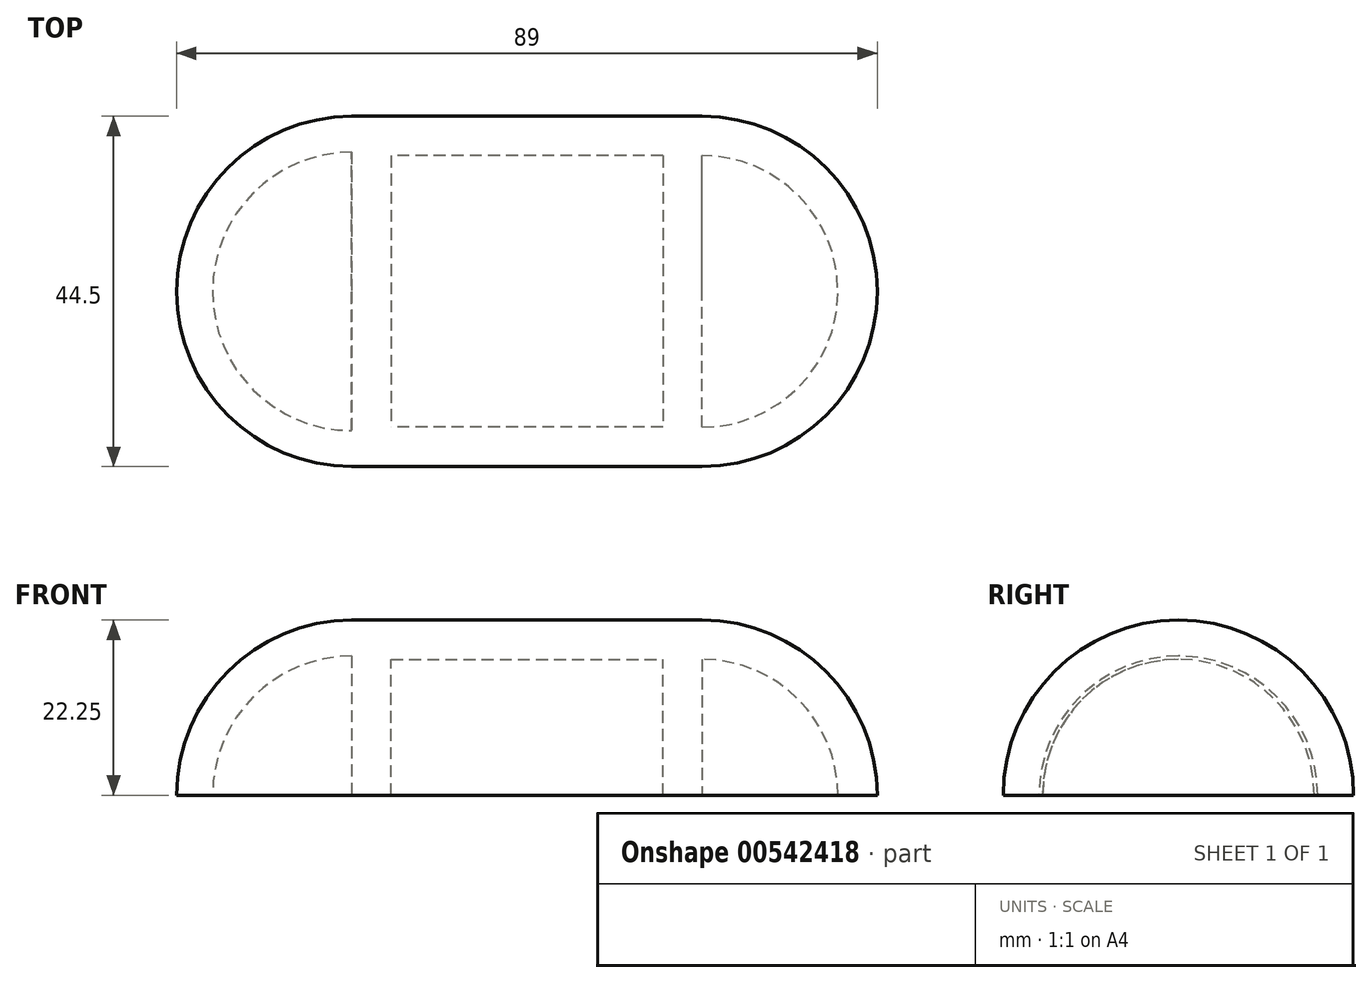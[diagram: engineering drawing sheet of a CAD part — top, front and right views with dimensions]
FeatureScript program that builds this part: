
annotation { "Feature Type Name" : "Feature", "Feature Type Description" : "" }
export const myFeature = defineFeature(function(context is Context, id is Id, definition is map)
    precondition{}
    {
        {
            var Q0;
            Q0=qCreatedBy(makeId("Top.planeOp"),FACE);
            var sketch = newSketch(context, id + "F0", { "sketchPlane" : qUnion([Q0])});
            skLineSegment(sketch, "E0.bottom", {"start": v(22.25, 22.25) * mm, "end": v(-22.25, 22.25) * mm});
            skLineSegment(sketch, "E0.top", {"start": v(22.25, -22.25) * mm, "end": v(-22.25, -22.25) * mm});
            skLineSegment(sketch, "E0.left", {"start": v(22.25, 22.25) * mm, "end": v(22.25, -22.25) * mm});
            skLineSegment(sketch, "E0.right", {"start": v(-22.25, 22.25) * mm, "end": v(-22.25, -22.25) * mm});
            skPoint(sketch, "E0.middle", {"position": v(0, 0) * mm});
            skLineSegment(sketch, "E1.bottom", {"start": v(17.25, -17.25) * mm, "end": v(-17.25, -17.25) * mm});
            skLineSegment(sketch, "E1.top", {"start": v(17.25, 17.25) * mm, "end": v(-17.25, 17.25) * mm});
            skLineSegment(sketch, "E1.left", {"start": v(17.25, -17.25) * mm, "end": v(17.25, 17.25) * mm});
            skLineSegment(sketch, "E1.right", {"start": v(-17.25, -17.25) * mm, "end": v(-17.25, 17.25) * mm});
            skLineSegment(sketch, "E2", {"start": v(-45.54, 0) * mm, "end": v(54.8, 0) * mm});
            skPoint(sketch, "E2.endSnap0", {"position": v(-22.25, 0) * mm});
            skSolve(sketch);
        }
        {
            var Q0;
            {var subQ1=sQuery(id+"F0.wireOp",EDGE,"E0.top");Q0=makeQuery(id+"F0.imprint","IMPRINT",FACE,{"disambiguationData":[TD([[makeQuery(id+"F0.imprint","IMPRINT",EDGE,{"derivedFrom":subQ1}),-1.0]])]});}
            var Q1;
            Q1=sQuery(id+"F0.wireOp",EDGE,"E2");
            revolve(context, id + "F1", {"entities" : qUnion([Q0]), "axis" : qUnion([Q1]), "revolveType" : RevolveType.ONE_DIRECTION, "oppositeDirection" : true, "angle" : 180 * degree});
        }
        {
            var Q0;
            Q0=makeQuery(id+"F1.opRevolve","SWEPT_FACE",FACE,{"disambiguationData":[OSD([sQuery(id+"F0.wireOp",EDGE,"E0.left")])]});
            var sketch = newSketch(context, id + "F2", { "sketchPlane" : qUnion([Q0])});
            skArc(sketch, "E3", {"start": v(-22.25, 0) * mm, "mid": v(-15.73, 15.73) * mm, "end": v(0, 22.25) * mm});
            skArc(sketch, "E4", {"start": v(-17.25, 0) * mm, "mid": v(-12.2, 12.2) * mm, "end": v(0, 17.25) * mm});
            skLineSegment(sketch, "E5", {"start": v(-32.26, 0) * mm, "end": v(44.71, 0) * mm});
            skLineSegment(sketch, "E6", {"start": v(0, 30.6) * mm, "end": v(0, -10.44) * mm});
            skSolve(sketch);
        }
        {
            var Q0;
            {var subQ0=sQuery(id+"F2.wireOp",EDGE,"E3");Q0=makeQuery(id+"F2.imprint","IMPRINT",FACE,{"disambiguationData":[TD([[makeQuery(id+"F2.imprint","IMPRINT",EDGE,{"derivedFrom":subQ0}),1.0]])]});}
            var Q1;
            Q1=sQuery(id+"F2.wireOp",EDGE,"E6");
            revolve(context, id + "F3", {"operationType" : NewBodyOperationType.ADD, "entities" : qUnion([Q0]), "axis" : qUnion([Q1]), "revolveType" : RevolveType.ONE_DIRECTION, "oppositeDirection" : true, "angle" : 180 * degree});
        }
        {
            var Q0;
            Q0=makeQuery(id+"F1.opRevolve","SWEPT_FACE",FACE,{"disambiguationData":[OSD([sQuery(id+"F0.wireOp",EDGE,"E0.right")])]});
            var sketch = newSketch(context, id + "F4", { "sketchPlane" : qUnion([Q0])});
            skArc(sketch, "E7", {"start": v(-22.25, 0) * mm, "mid": v(-15.73, 15.73) * mm, "end": v(0, 22.25) * mm});
            skArc(sketch, "E8", {"start": v(-17.69, 0) * mm, "mid": v(-12.5, 12.5) * mm, "end": v(0, 17.69) * mm});
            skLineSegment(sketch, "E9", {"start": v(0, 29.25) * mm, "end": v(0, -17) * mm});
            skLineSegment(sketch, "E10", {"start": v(-35.24, 0) * mm, "end": v(52.52, 0) * mm});
            skSolve(sketch);
        }
        {
            var Q0;
            {var subQ0=sQuery(id+"F4.wireOp",EDGE,"E7");Q0=makeQuery(id+"F4.imprint","IMPRINT",FACE,{"disambiguationData":[TD([[makeQuery(id+"F4.imprint","IMPRINT",EDGE,{"derivedFrom":subQ0}),-1.0]])]});}
            var Q1;
            Q1=sQuery(id+"F4.wireOp",EDGE,"E9");
            revolve(context, id + "F5", {"operationType" : NewBodyOperationType.ADD, "entities" : qUnion([Q0]), "axis" : qUnion([Q1]), "revolveType" : RevolveType.ONE_DIRECTION, "oppositeDirection" : true, "angle" : 180 * degree});
        }
    });
